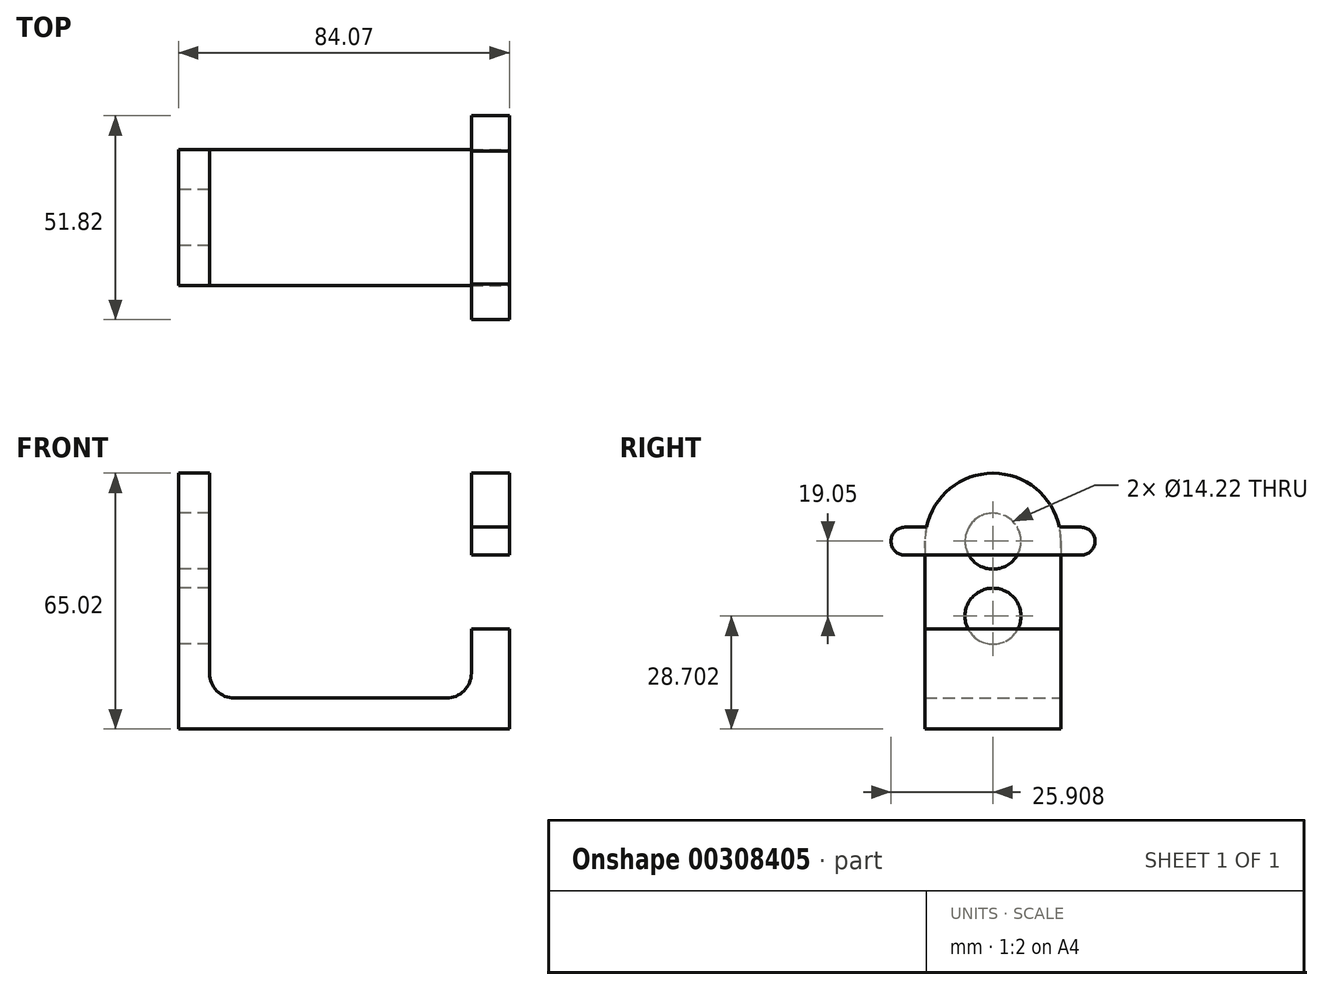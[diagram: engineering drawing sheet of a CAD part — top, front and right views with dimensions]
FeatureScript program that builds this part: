
annotation { "Feature Type Name" : "Feature", "Feature Type Description" : "" }
export const myFeature = defineFeature(function(context is Context, id is Id, definition is map)
    precondition{}
    {
        {
            var Q0;
            Q0=qCreatedBy(makeId("Front.planeOp"),FACE);
            var sketch = newSketch(context, id + "F0", { "sketchPlane" : qUnion([Q0])});
            skLineSegment(sketch, "E0", {"start": v(0, 25.4) * mm, "end": v(0, 0) * mm});
            skLineSegment(sketch, "E1", {"start": v(0, 0) * mm, "end": v(-84.07, 0) * mm});
            skLineSegment(sketch, "E2", {"start": v(-84.07, 0) * mm, "end": v(-84.07, 47.75) * mm});
            skLineSegment(sketch, "E3", {"start": v(-84.07, 47.75) * mm, "end": v(-76.2, 47.75) * mm});
            skLineSegment(sketch, "E4", {"start": v(-76.2, 47.75) * mm, "end": v(-76.2, 7.87) * mm});
            skLineSegment(sketch, "E5", {"start": v(-76.2, 7.87) * mm, "end": v(-9.65, 7.87) * mm});
            skLineSegment(sketch, "E6", {"start": v(-9.65, 7.87) * mm, "end": v(-9.65, 25.4) * mm});
            skLineSegment(sketch, "E7", {"start": v(-9.65, 25.4) * mm, "end": v(0, 25.4) * mm});
            skSolve(sketch);
        }
        {
            var Q0;
            Q0=makeQuery(id+"F0.imprint","IMPRINT",FACE,{"disambiguationData":[TD([[makeQuery(id+"F0.imprint","IMPRINT",EDGE,{"derivedFrom":sQuery(id+"F0.wireOp",EDGE,"E0")}),-1.0]])]});
            extrude(context, id + "F1", {"entities" : qUnion([Q0]), "depth" : 34.54 * mm});
        }
        {
            var Q0;
            Q0=makeQuery(id+"F1.opExtrude","SWEPT_FACE",FACE,{"disambiguationData":[OSD([sQuery(id+"F0.wireOp",EDGE,"E2")])]});
            var sketch = newSketch(context, id + "F2", { "sketchPlane" : qUnion([Q0])});
            skLineSegment(sketch, "E8.0", {"start": v(0, 0) * mm, "end": v(0, 47.75) * mm});
            skLineSegment(sketch, "E9.0", {"start": v(34.54, 0) * mm, "end": v(34.54, 47.75) * mm});
            skLineSegment(sketch, "E10.0", {"start": v(34.54, 47.75) * mm, "end": v(0, 47.75) * mm});
            skArc(sketch, "E11", {"start": v(34.54, 47.75) * mm, "mid": v(17.27, 65.02) * mm, "end": v(0, 47.75) * mm});
            skSolve(sketch);
        }
        {
            var Q0;
            Q0=makeQuery(id+"F2.imprint","IMPRINT",FACE,{"disambiguationData":[TD([[makeQuery(id+"F2.imprint","IMPRINT",EDGE,{"derivedFrom":sQuery(id+"F2.wireOp",EDGE,"E10.0")}),-1.0]])]});
            extrude(context, id + "F3", {"entities" : qUnion([Q0]), "operationType" : NewBodyOperationType.ADD, "oppositeDirection" : true, "depth" : 7.87 * mm});
        }
        {
            var Q0;
            Q0=makeQuery(id+"F1.opExtrude","SWEPT_FACE",FACE,{"disambiguationData":[OSD([sQuery(id+"F0.wireOp",EDGE,"E0")])]});
            var sketch = newSketch(context, id + "F4", { "sketchPlane" : qUnion([Q0])});
            skLineSegment(sketch, "E12", {"start": v(-39.62, 47.75) * mm, "end": v(5.08, 47.75) * mm, "construction": true});
            skArc(sketch, "E13.0.startCap", {"start": v(-39.62, 44.2) * mm, "mid": v(-43.18, 47.75) * mm, "end": v(-39.62, 51.3) * mm});
            skArc(sketch, "E13.0.endCap", {"start": v(5.08, 51.3) * mm, "mid": v(8.64, 47.75) * mm, "end": v(5.08, 44.2) * mm});
            skLineSegment(sketch, "E13.0.left", {"start": v(-39.62, 51.3) * mm, "end": v(5.08, 51.3) * mm});
            skLineSegment(sketch, "E13.0.right", {"start": v(-39.62, 44.2) * mm, "end": v(5.08, 44.2) * mm});
            skLineSegment(sketch, "E14", {"start": v(-17.27, 61.24) * mm, "end": v(-17.27, 31.66) * mm, "construction": true});
            skLineSegment(sketch, "E15.0", {"start": v(-34.54, 25.4) * mm, "end": v(-34.54, 0) * mm});
            skArc(sketch, "E16", {"start": v(-34.54, 25.4) * mm, "mid": v(-36.4, 29.44) * mm, "end": v(-40.68, 30.67) * mm});
            skArc(sketch, "E17", {"start": v(-40.68, 30.67) * mm, "mid": v(-60.48, 46.46) * mm, "end": v(-43.26, 65.02) * mm});
            skLineSegment(sketch, "E18", {"start": v(-43.26, 65.02) * mm, "end": v(6.88, 65.02) * mm});
            skArc(sketch, "E19", {"start": v(6.88, 65.02) * mm, "mid": v(24.15, 47.8) * mm, "end": v(6.96, 30.48) * mm});
            skLineSegment(sketch, "E20.0", {"start": v(0, 25.4) * mm, "end": v(0, 0) * mm});
            skArc(sketch, "E21", {"start": v(0, 25.4) * mm, "mid": v(2.19, 29.7) * mm, "end": v(6.96, 30.48) * mm});
            skArc(sketch, "E22.0", {"start": v(-34.54, 47.75) * mm, "mid": v(-17.27, 65.02) * mm, "end": v(0, 47.75) * mm});
            skSolve(sketch);
        }
        {
            var Q0;
            {var subQ5=sQuery(id+"F4.wireOp",EDGE,"E13.0.startCap");Q0=makeQuery(id+"F4.imprint","IMPRINT",FACE,{"disambiguationData":[TD([[makeQuery(id+"F4.imprint","IMPRINT",EDGE,{"derivedFrom":subQ5}),1.0]])]});}
            var Q1;
            {var subQ0=sQuery(id+"F4.wireOp",EDGE,"E22.0");var subQ1=sQuery(id+"F4.wireOp",EDGE,"E13.0.left");var subQ2=makeQuery(id+"F4.imprint","INTERSECT",VERTEX,{"disambiguationData":[OD(0.0)],"derivedFrom":[subQ1,subQ0]});Q1=makeQuery(id+"F4.imprint","IMPRINT",FACE,{"disambiguationData":[TD([[makeQuery(id+"F4.imprint","IMPRINT",EDGE,{"disambiguationData":[TD([[subQ2,-1.0]])],"derivedFrom":subQ1}),1.0]])]});}
            extrude(context, id + "F5", {"entities" : qUnion([Q0, Q1]), "operationType" : NewBodyOperationType.ADD, "oppositeDirection" : true, "depth" : 9.65 * mm});
        }
        {
            var Q0;
            Q0=makeQuery(id+"F3.boolean.opBoolean","MERGE",FACE,{"derivedFrom":[makeQuery(id+"F1.opExtrude","SWEPT_FACE",FACE,{"disambiguationData":[OSD([sQuery(id+"F0.wireOp",EDGE,"E2")])]}),makeQuery(id+"F3.opExtrude","CAP_FACE",FACE,{"disambiguationData":[OSD([sQuery(id+"F2.wireOp",EDGE,"E10.0"),sQuery(id+"F2.wireOp",EDGE,"E11")])],"isStart":true})]});
            var sketch = newSketch(context, id + "F6", { "sketchPlane" : qUnion([Q0])});
            skCircle(sketch, "E23", {"center": v(17.27, 47.75) * mm, "radius": 7.11 * mm});
            skCircle(sketch, "E24", {"center": v(17.27, 28.7) * mm, "radius": 7.11 * mm});
            skSolve(sketch);
        }
        {
            var Q0;
            Q0=makeQuery(id+"F6.imprint","IMPRINT",FACE,{"disambiguationData":[TD([[makeQuery(id+"F6.imprint","IMPRINT",EDGE,{"derivedFrom":sQuery(id+"F6.wireOp",EDGE,"E23")}),1.0]])]});
            var Q1;
            Q1=makeQuery(id+"F6.imprint","IMPRINT",FACE,{"disambiguationData":[TD([[makeQuery(id+"F6.imprint","IMPRINT",EDGE,{"derivedFrom":sQuery(id+"F6.wireOp",EDGE,"E24")}),1.0]])]});
            extrude(context, id + "F7", {"entities" : qUnion([Q0, Q1]), "operationType" : NewBodyOperationType.REMOVE, "oppositeDirection" : true, "depth" : 25.4 * mm});
        }
        {
            var Q0;
            Q0=makeQuery(id+"F1.opExtrude","SWEPT_EDGE",EDGE,{"disambiguationData":[OSD([sQuery(id+"F0.wireOp",EDGE,"E5"),sQuery(id+"F0.wireOp",EDGE,"E6")])]});
            var Q1;
            Q1=makeQuery(id+"F1.opExtrude","SWEPT_EDGE",EDGE,{"disambiguationData":[OSD([sQuery(id+"F0.wireOp",EDGE,"E4"),sQuery(id+"F0.wireOp",EDGE,"E5")])]});
            fillet(context, id + "F8", {"entities" : qUnion([Q0, Q1]), "radius" : 6.35 * mm, "tangentPropagation" : true, "allowEdgeOverflow" : false});
        }
    });
